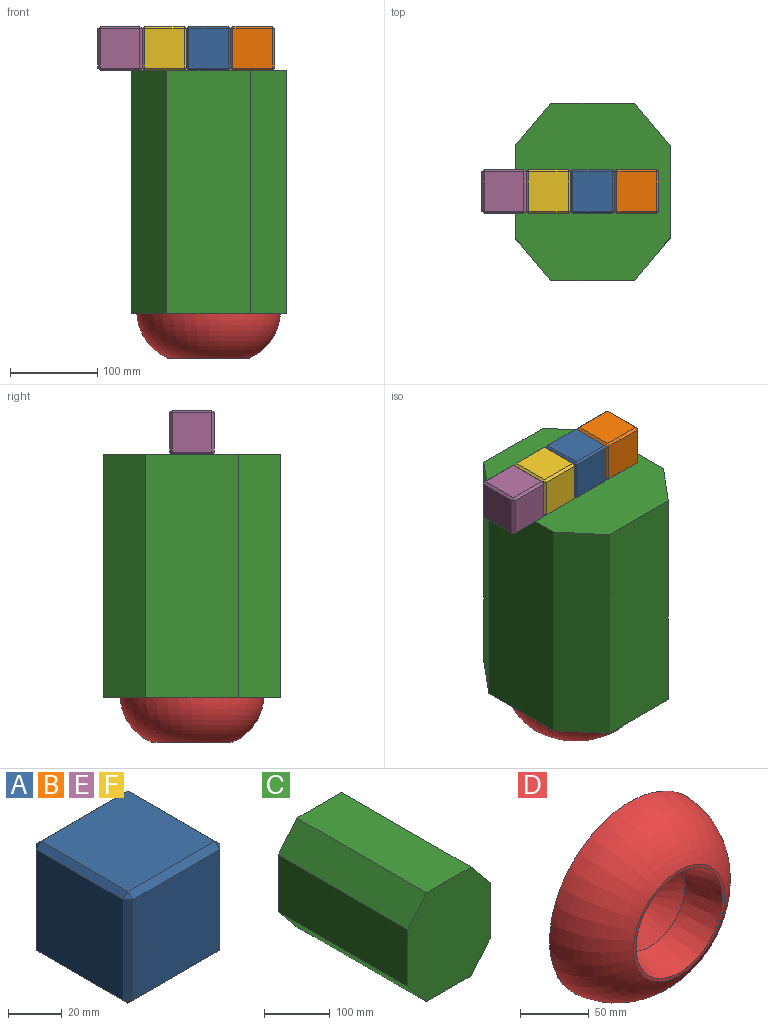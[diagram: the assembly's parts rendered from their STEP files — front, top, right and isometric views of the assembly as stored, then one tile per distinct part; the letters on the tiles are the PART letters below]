
ASSEMBLY  parts=6 mates=5
PART A: 26 faces, bbox 50.8x50.8x50.8 mm
  f0: plane 45.72x45.72mm, normal (0,1,0), area 2090.3mm2, adj f6,f10,f11,f12
  f1: plane 45.72x45.72mm, normal (-1,0,0), area 2090.3mm2, adj f6,f9,f13,f14
  f2: plane 45.72x45.72mm, normal (0,-1,0), area 2090.3mm2, adj f14,f19,f22,f25
  f3: plane 45.72x45.72mm, normal (1,0,0), area 2090.3mm2, adj f11,f20,f21,f25
  f4: plane 45.72x45.72mm, normal (0,0,1), area 2090.3mm2, adj f9,f10,f19,f20
  f5: plane 45.72x45.72mm, normal (0,0,-1), area 2090.3mm2, adj f12,f13,f21,f22
  f6: plane 45.72x2.54mm, normal (-0.71,0.71,0), area 164.2mm2, adj f0,f1,f7,f8
  f7: plane 2.54x2.54mm, normal (-0.58,0.58,0.58), area 5.6mm2, adj f6,f9,f10
  f8: plane 2.54x2.54mm, normal (-0.58,0.58,-0.58), area 5.6mm2, adj f6,f12,f13
  f9: plane 45.72x2.54mm, normal (-0.71,0,0.71), area 164.2mm2, adj f1,f4,f7,f15
  f10: plane 45.72x2.54mm, normal (0,0.71,0.71), area 164.2mm2, adj f0,f4,f7,f16
  f11: plane 45.72x2.54mm, normal (0.71,0.71,0), area 164.2mm2, adj f0,f3,f16,f17
  f12: plane 45.72x2.54mm, normal (0,0.71,-0.71), area 164.2mm2, adj f0,f5,f8,f17
  f13: plane 45.72x2.54mm, normal (-0.71,0,-0.71), area 164.2mm2, adj f1,f5,f8,f18
  f14: plane 45.72x2.54mm, normal (-0.71,-0.71,0), area 164.2mm2, adj f1,f2,f15,f18
  f15: plane 2.54x2.54mm, normal (-0.58,-0.58,0.58), area 5.6mm2, adj f9,f14,f19
  f16: plane 2.54x2.54mm, normal (0.58,0.58,0.58), area 5.6mm2, adj f10,f11,f20
  f17: plane 2.54x2.54mm, normal (0.58,0.58,-0.58), area 5.6mm2, adj f11,f12,f21
  f18: plane 2.54x2.54mm, normal (-0.58,-0.58,-0.58), area 5.6mm2, adj f13,f14,f22
  f19: plane 45.72x2.54mm, normal (0,-0.71,0.71), area 164.2mm2, adj f2,f4,f15,f23
  f20: plane 45.72x2.54mm, normal (0.71,0,0.71), area 164.2mm2, adj f3,f4,f16,f23
  f21: plane 45.72x2.54mm, normal (0.71,0,-0.71), area 164.2mm2, adj f3,f5,f17,f24
  f22: plane 45.72x2.54mm, normal (0,-0.71,-0.71), area 164.2mm2, adj f2,f5,f18,f24
  f23: plane 2.54x2.54mm, normal (0.58,-0.58,0.58), area 5.6mm2, adj f19,f20,f25
  f24: plane 2.54x2.54mm, normal (0.58,-0.58,-0.58), area 5.6mm2, adj f21,f22,f25
  f25: plane 45.72x2.54mm, normal (0.71,-0.71,0), area 164.2mm2, adj f2,f3,f23,f24
PART B: same geometry as A
PART C: 10 faces, bbox 177.8x279.4x203.2 mm
  f0: plane 279.4x48.64mm, normal (-0.77,0,0.64), area 17741.9mm2, adj f1,f7,f8,f9
  f1: plane 279.4x105.91mm, normal (-1,0,0), area 29591.9mm2, adj f0,f2,f8,f9
  f2: plane 279.4x48.64mm, normal (-0.77,0,-0.64), area 17741.9mm2, adj f1,f3,f8,f9
  f3: plane 279.4x96.17mm, normal (0,0,-1), area 26868.8mm2, adj f2,f4,f8,f9
  f4: plane 279.4x48.64mm, normal (0.77,0,-0.64), area 17741.9mm2, adj f3,f5,f8,f9
  f5: plane 279.4x105.91mm, normal (1,0,0), area 29591.9mm2, adj f4,f6,f8,f9
  f6: plane 279.4x48.64mm, normal (0.77,0,0.64), area 17741.9mm2, adj f5,f7,f8,f9
  f7: plane 279.4x96.17mm, normal (0,0,1), area 26868.8mm2, adj f0,f6,f8,f9
  f8: plane 203.2x177.8mm, normal (0,1,0), area 32158mm2, adj f0,f1,f2,f3,f4,f5,f6,f7
  f9: plane 203.2x177.8mm, normal (0,-1,0), area 32158mm2, adj f0,f1,f2,f3,f4,f5,f6,f7
PART D: 6 faces, bbox 164.8x50.8x164.8 mm
  f0: torus R=23.07mm, axis (0,-1,0), area 28423.7mm2, adj f1,f5
  f1: plane 93.85x93.85mm, normal (0,-1,0), area 749.8mm2, adj f0,f2
  f2: cone r=44.31mm half-angle=14.3deg, axis (0,-1,0), area 7982mm2, adj f1,f3
  f3: cone r=36.52mm half-angle=55.9deg, axis (0,-1,0), area 4310mm2, adj f2,f4
  f4: cylinder r=14.09mm len=28.18mm, axis (0,-1,0), area 454.6mm2, adj f3,f5
  f5: plane 164.81x164.81mm, normal (0,1,0), area 20710.8mm2, adj f0,f4
PART E: same geometry as A
PART F: same geometry as A
PLACE A t=(-2.4,219.34,145.21)mm
PLACE B t=(48.4,219.34,145.21)mm
PLACE C rot(axis=(1,0,0),90deg) t=(-2.4,219.34,-134.19)mm
PLACE D rot(axis=(1,0,0),90deg) t=(-2.4,219.34,-134.19)mm
PLACE E t=(-104,219.34,145.21)mm
PLACE F t=(-53.2,219.34,145.21)mm
MATE fastened D.f0 <-> C.f9  axis (0,0,-1) through (-2.4,219.34,-134.19)mm
MATE fastened B.f1 <-> A.f3  axis (1,0,0) through (23,219.34,170.61)mm
MATE fastened F.f3 <-> A.f1  axis (1,0,0) through (-27.8,219.34,170.61)mm
MATE fastened A.f5 <-> C.f8  axis (0,0,1) through (-2.4,219.34,145.21)mm
MATE fastened E.f3 <-> F.f1  axis (1,0,0) through (-78.6,219.34,170.61)mm
